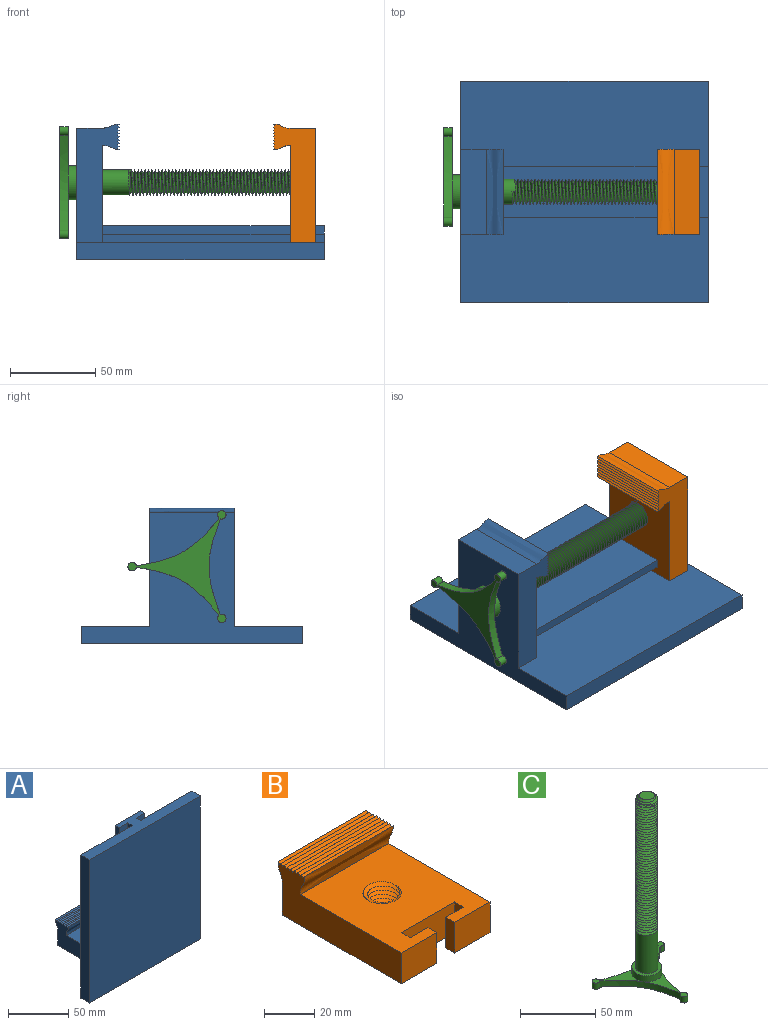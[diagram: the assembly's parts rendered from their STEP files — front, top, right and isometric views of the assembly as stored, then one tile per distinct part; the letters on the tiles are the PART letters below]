
ASSEMBLY  parts=3 mates=3
PART A: 37 faces, bbox 130x79.7x145 mm
  f0: plane 145x60.1mm, normal (0,1,0), area 8413mm2, adj f7,f8,f12,f13,f33,f35
  f1: plane 130x5.2mm, normal (1,0,0), area 676mm2, adj f2,f11,f12,f33
  f2: plane 130x10mm, normal (0,-1,0), area 1300mm2, adj f1,f3,f12,f33
  f3: plane 130x4.8mm, normal (1,0,0), area 624mm2, adj f2,f4,f12,f33
  f4: plane 130x29.8mm, normal (0,1,0), area 3874mm2, adj f3,f5,f12,f33
  f5: plane 130x4.8mm, normal (-1,0,0), area 624mm2, adj f4,f6,f12,f33
  f6: plane 130x10mm, normal (0,-1,0), area 1300mm2, adj f5,f7,f12,f33
  f7: plane 130x5.2mm, normal (-1,0,0), area 676mm2, adj f0,f6,f12,f33
  f8: plane 145x10mm, normal (-1,0,0), area 1450mm2, adj f0,f9,f12,f13
  f9: plane 145x130mm, normal (0,-1,0), area 18850mm2, adj f8,f10,f12,f13
  f10: plane 145x10mm, normal (1,0,0), area 1450mm2, adj f9,f11,f12,f13
  f11: plane 145x60.1mm, normal (0,1,0), area 8413mm2, adj f1,f10,f12,f13,f14,f33
  f12: plane 130x20mm, normal (0,0,1), area 1494mm2, adj f0,f1,f2,f3,f4,f5,f6,f7
  f13: plane 130x77.15mm, normal (0,0,-1), area 4476mm2, adj f0,f8,f9,f10,f11,f14,f32,f35
  f14: plane 69.65x25mm, normal (1,0,0), area 1124.8mm2, adj f11,f13,f15,f16,f17,f18,f19,f20
  f15: plane 50x1mm, normal (0,0.73,0.68), area 68.5mm2, adj f14,f16,f34,f35
  f16: plane 50x1mm, normal (0,-0.73,0.68), area 68.5mm2, adj f14,f15,f17,f35
  f17: plane 50x1mm, normal (0,0.73,0.68), area 68.5mm2, adj f14,f16,f18,f35
  f18: plane 50x1mm, normal (0,-0.73,0.68), area 68.5mm2, adj f14,f17,f19,f35
  f19: plane 50x1mm, normal (0,0.73,0.68), area 68.5mm2, adj f14,f18,f20,f35
  f20: plane 50x1mm, normal (0,-0.73,0.68), area 68.5mm2, adj f14,f19,f21,f35
  f21: plane 50x1mm, normal (0,0.73,0.68), area 68.5mm2, adj f14,f20,f22,f35
  f22: plane 50x1mm, normal (0,-0.73,0.68), area 68.5mm2, adj f14,f21,f23,f35
  f23: plane 50x1mm, normal (0,0.73,0.68), area 68.5mm2, adj f14,f22,f24,f35
  f24: plane 50x1mm, normal (0,-0.73,0.68), area 68.5mm2, adj f14,f23,f25,f35
  f25: plane 50x1mm, normal (0,0.73,0.68), area 68.5mm2, adj f14,f24,f26,f35
  f26: plane 50x1mm, normal (0,-0.73,0.68), area 68.5mm2, adj f14,f25,f27,f35
  f27: plane 50x1mm, normal (0,0.73,0.68), area 68.5mm2, adj f14,f26,f28,f35
  f28: plane 50x1mm, normal (0,-0.73,0.68), area 68.5mm2, adj f14,f27,f29,f35
  f29: plane 50x1mm, normal (0,0.73,0.68), area 68.5mm2, adj f14,f28,f30,f35
  f30: plane 50x1mm, normal (0,-0.73,0.68), area 68.5mm2, adj f14,f29,f31,f35
  f31: extruded ~50x10mm, area 521.4mm2, adj f14,f30,f32,f35
  f32: plane 50x15mm, normal (0,1,0), area 750mm2, adj f13,f14,f31,f35
  f33: plane 57.15x50mm, normal (0,0,1), area 2482mm2, adj f0,f1,f2,f3,f4,f5,f6,f7
  f34: extruded ~50x10mm, area 521.4mm2, adj f14,f15,f33,f35
  f35: plane 69.65x25mm, normal (-1,0,0), area 1124.8mm2, adj f0,f13,f15,f16,f17,f18,f19,f20
  f36: cylinder r=7.6mm len=15.2mm, axis (0,0,-1), area 716.3mm2, adj f13,f33
PART B: 34 faces, bbox 50x69.7x26 mm
  f0: plane 57.15x50mm, normal (0,0,1), area 2477.1mm2, adj f2,f3,f4,f5,f6,f7,f8,f9
  f1: plane 67.15x50mm, normal (0,0,-1), area 2977mm2, adj f2,f3,f4,f5,f6,f7,f8,f9
  f2: bspline ~20.09x17.4mm, area 897.5mm2, adj f0,f1,f3
  f3: bspline ~20.09x17.4mm, area 897.5mm2, adj f0,f1,f2
  f4: plane 69.65x25mm, normal (-1,0,0), area 1124.7mm2, adj f0,f1,f5,f15,f16,f17,f18,f19
  f5: plane 20x15mm, normal (0,-1,0), area 300mm2, adj f0,f1,f4,f6
  f6: plane 15x5mm, normal (1,0,0), area 75mm2, adj f0,f1,f5,f7
  f7: plane 15x10mm, normal (0,1,0), area 150mm2, adj f0,f1,f6,f8
  f8: plane 15x5mm, normal (1,0,0), area 75mm2, adj f0,f1,f7,f9
  f9: plane 30x15mm, normal (0,-1,0), area 450mm2, adj f0,f1,f8,f10
  f10: plane 15x5mm, normal (-1,0,0), area 75mm2, adj f0,f1,f9,f11
  f11: plane 15x10mm, normal (0,1,0), area 150mm2, adj f0,f1,f10,f12
  f12: plane 15x5mm, normal (-1,0,0), area 75mm2, adj f0,f1,f11,f13
  f13: plane 20x15mm, normal (0,-1,0), area 300mm2, adj f0,f1,f12,f14
  f14: plane 69.65x25mm, normal (1,0,0), area 1124.7mm2, adj f0,f1,f13,f15,f16,f17,f18,f19
  f15: extruded ~50x10mm, area 521.4mm2, adj f0,f4,f14,f16
  f16: plane 50x1mm, normal (0,0.73,0.68), area 68.5mm2, adj f4,f14,f15,f17
  f17: plane 50x1mm, normal (0,-0.73,0.68), area 68.5mm2, adj f4,f14,f16,f18
  f18: plane 50x1mm, normal (0,0.73,0.68), area 68.5mm2, adj f4,f14,f17,f19
  f19: plane 50x1mm, normal (0,-0.73,0.68), area 68.5mm2, adj f4,f14,f18,f20
  f20: plane 50x1mm, normal (0,0.73,0.68), area 68.5mm2, adj f4,f14,f19,f21
  f21: plane 50x1mm, normal (0,-0.73,0.68), area 68.5mm2, adj f4,f14,f20,f22
  f22: plane 50x1mm, normal (0,0.73,0.68), area 68.5mm2, adj f4,f14,f21,f23
  f23: plane 50x1mm, normal (0,-0.73,0.68), area 68.5mm2, adj f4,f14,f22,f24
  f24: plane 50x1mm, normal (0,0.73,0.68), area 68.5mm2, adj f4,f14,f23,f25
  f25: plane 50x1mm, normal (0,-0.73,0.68), area 68.5mm2, adj f4,f14,f24,f26
  f26: plane 50x1mm, normal (0,0.73,0.68), area 68.5mm2, adj f4,f14,f25,f27
  f27: plane 50x1mm, normal (0,-0.73,0.68), area 68.5mm2, adj f4,f14,f26,f28
  f28: plane 50x1mm, normal (0,0.73,0.68), area 68.5mm2, adj f4,f14,f27,f29
  f29: plane 50x1mm, normal (0,-0.73,0.68), area 68.5mm2, adj f4,f14,f28,f30
  f30: plane 50x1mm, normal (0,0.73,0.68), area 68.5mm2, adj f4,f14,f29,f31
  f31: plane 50x1mm, normal (0,-0.73,0.68), area 68.5mm2, adj f4,f14,f30,f32
  f32: extruded ~50x10mm, area 521.4mm2, adj f4,f14,f31,f33
  f33: plane 50x15mm, normal (0,1,0), area 750mm2, adj f1,f4,f14,f32
PART C: 18 faces, bbox 65.6x57.5x151.3 mm
  f0: cylinder r=7.45mm len=32mm, axis (0,0,-1), area 1451.1mm2, adj f1,f3,f7
  f1: plane 2.3x2mm, normal (0,1,0), area 2.3mm2, adj f0,f2,f3
  f2: bspline ~110.33x17.21mm, area 5349.9mm2, adj f1,f3,f5
  f3: bspline ~110.33x17.21mm, area 5414.1mm2, adj f0,f1,f2,f5
  f4: plane 10.3x10.3mm, normal (0,0,1), area 83.3mm2, adj f5
  f5: cone r=5.15mm half-angle=45deg, axis (0,0,-1), area 60.4mm2, adj f2,f3,f4
  f6: cylinder r=10mm len=20mm, axis (0,0,-1), area 314.2mm2, adj f7,f8,f9,f10
  f7: plane 20x20mm, normal (0,0,1), area 139.8mm2, adj f0,f6
  f8: plane 33.54x25.72mm, normal (0,0,1), area 157.1mm2, adj f6,f11,f12,f13
  f9: plane 33.22x18.77mm, normal (0,0,1), area 157.1mm2, adj f6,f13,f14,f15
  f10: plane 33.54x25.72mm, normal (0,0,1), area 157.1mm2, adj f6,f11,f15,f16
  f11: extruded ~55.89x6.69mm, area 289.2mm2, adj f8,f10,f12,f16,f17
  f12: cylinder r=2.5mm len=5mm, axis (0,0,1), area 73.7mm2, adj f8,f11,f13,f17
  f13: extruded ~48.4x27.94mm, area 289.2mm2, adj f8,f9,f12,f14,f17
  f14: cylinder r=2.5mm len=5mm, axis (0,0,1), area 73.7mm2, adj f9,f13,f15,f17
  f15: extruded ~48.4x27.94mm, area 289.2mm2, adj f9,f10,f14,f16,f17
  f16: cylinder r=2.5mm len=5mm, axis (0,0,1), area 73.7mm2, adj f10,f11,f15,f17
  f17: plane 65.62x57.5mm, normal (0,0,-1), area 785.6mm2, adj f11,f12,f13,f14,f15,f16
PLACE A rot(axis=(0.58,0.58,0.58),120deg) t=(-145,-145,205)mm
PLACE B rot(axis=(0.58,-0.58,-0.58),120deg) t=(-5,15,45)mm
PLACE C rot(axis=(-0.71,0,-0.71),180deg) t=(-150,-64.94,45.32)mm
MATE cylindrical C.f0 <-> B.f1  axis (1,0,0) through (-5,-64.94,45.32)mm
MATE slider A.f12 <-> B.f0  axis (1,0,0) through (0,-65,20)mm
MATE planar A.f36 <-> C.f6  axis (-1,0,0) through (-145,-65,45)mm
